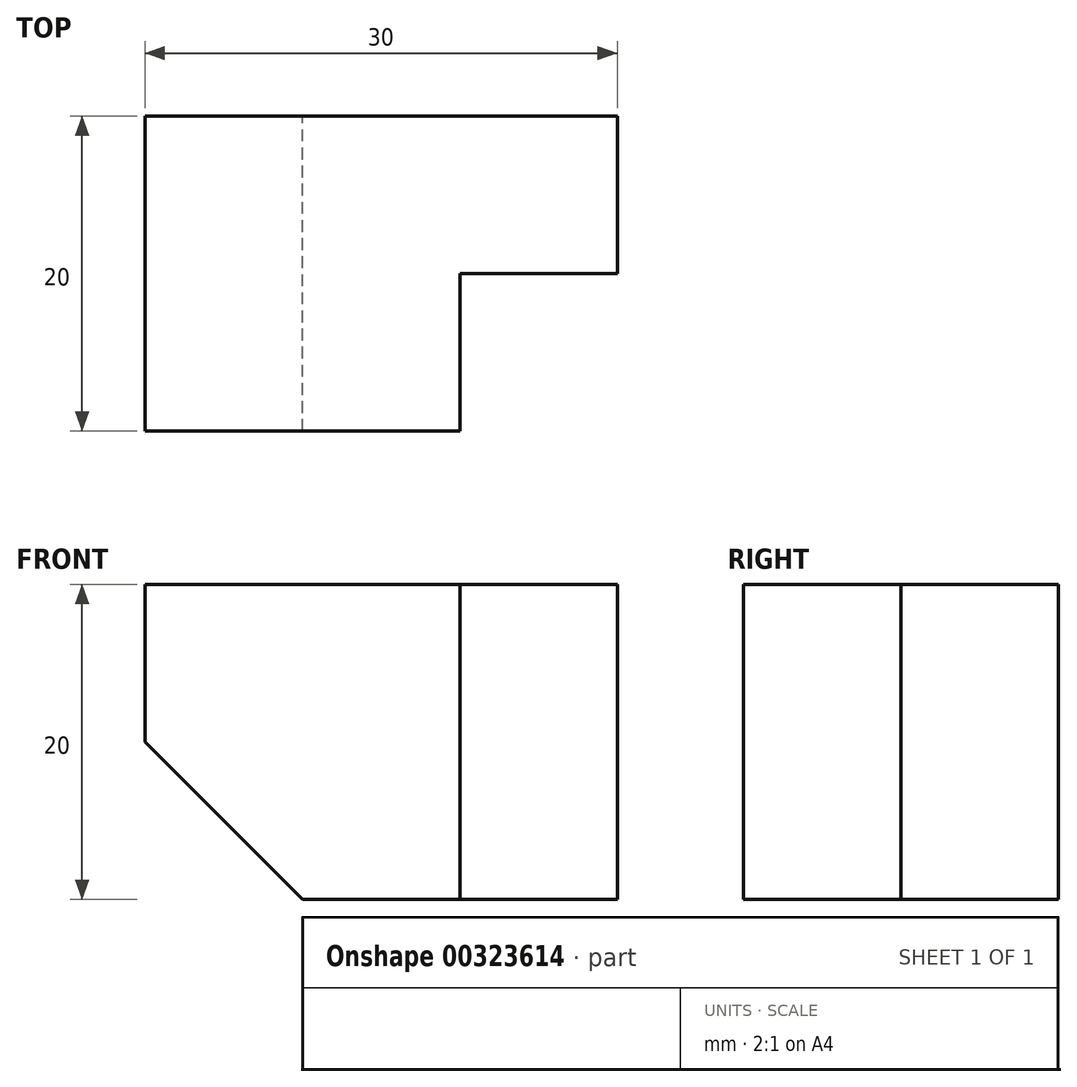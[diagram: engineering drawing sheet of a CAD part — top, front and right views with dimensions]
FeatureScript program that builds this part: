
annotation { "Feature Type Name" : "Feature", "Feature Type Description" : "" }
export const myFeature = defineFeature(function(context is Context, id is Id, definition is map)
    precondition{}
    {
        {
            var Q0;
            Q0=qCreatedBy(makeId("Front.planeOp"),FACE);
            var sketch = newSketch(context, id + "F0", { "sketchPlane" : qUnion([Q0])});
            skLineSegment(sketch, "E0", {"start": v(0, 0) * mm, "end": v(20, 0) * mm});
            skLineSegment(sketch, "E1", {"start": v(20, 0) * mm, "end": v(20, -20) * mm});
            skLineSegment(sketch, "E2", {"start": v(20, -20) * mm, "end": v(10, -20) * mm});
            skLineSegment(sketch, "E3", {"start": v(10, -20) * mm, "end": v(0, -10) * mm});
            skLineSegment(sketch, "E4", {"start": v(0, -10) * mm, "end": v(0, 0) * mm});
            skSolve(sketch);
        }
        {
            var Q0;
            Q0=qSketchRegion(id+"F0",true);
            extrude(context, id + "F1", {"entities" : qUnion([Q0]), "depth" : 20 * mm});
        }
        {
            var Q0;
            Q0=qCreatedBy(makeId("Front.planeOp"),FACE);
            var sketch = newSketch(context, id + "F2", { "sketchPlane" : qUnion([Q0])});
            skLineSegment(sketch, "E5", {"start": v(20, 0) * mm, "end": v(20, -20) * mm});
            skLineSegment(sketch, "E6", {"start": v(20, -20) * mm, "end": v(30, -20) * mm});
            skLineSegment(sketch, "E7", {"start": v(30, -20) * mm, "end": v(30, 0) * mm});
            skLineSegment(sketch, "E8", {"start": v(30, 0) * mm, "end": v(20, 0) * mm});
            skSolve(sketch);
        }
        {
            var Q0;
            Q0=qSketchRegion(id+"F2",true);
            extrude(context, id + "F3", {"entities" : qUnion([Q0]), "operationType" : NewBodyOperationType.ADD, "depth" : 10 * mm});
        }
    });
